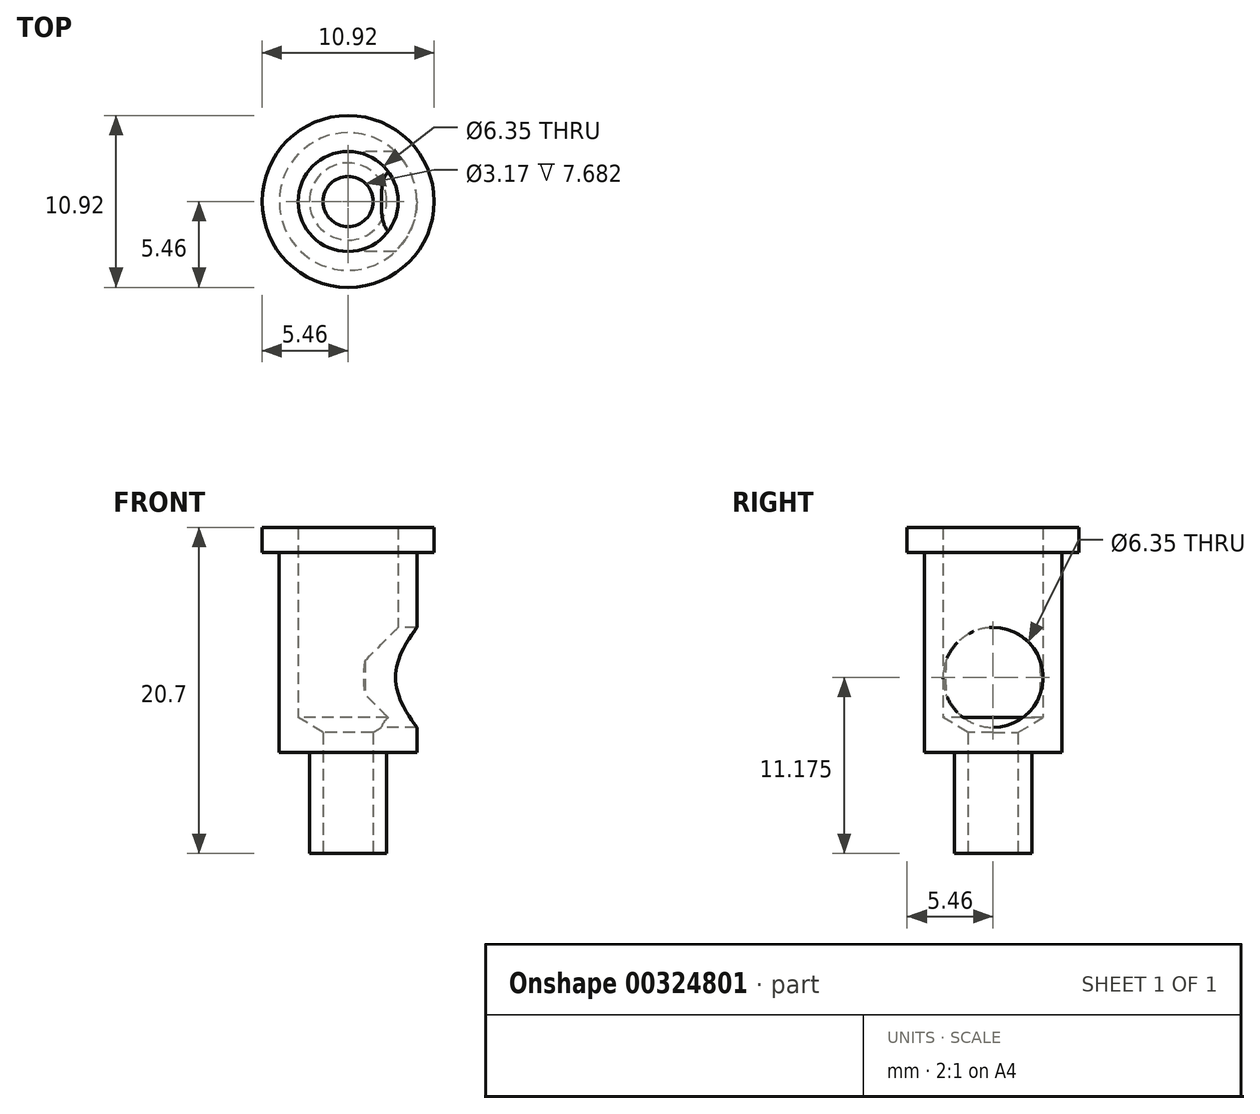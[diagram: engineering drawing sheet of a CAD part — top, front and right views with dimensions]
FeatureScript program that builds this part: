
annotation { "Feature Type Name" : "Feature", "Feature Type Description" : "" }
export const myFeature = defineFeature(function(context is Context, id is Id, definition is map)
    precondition{}
    {
        {
            var Q0;
            Q0=qCreatedBy(makeId("Top.planeOp"),FACE);
            var sketch = newSketch(context, id + "F0", { "sketchPlane" : qUnion([Q0])});
            skCircle(sketch, "E0", {"center": v(0, 0) * mm, "radius": 4.37 * mm});
            skSolve(sketch);
        }
        {
            var Q0;
            Q0=makeQuery(id+"F0.imprint","IMPRINT",FACE,{"disambiguationData":[TD([[makeQuery(id+"F0.imprint","IMPRINT",EDGE,{"derivedFrom":sQuery(id+"F0.wireOp",EDGE,"E0")}),1.0]])]});
            extrude(context, id + "F1", {"entities" : qUnion([Q0]), "depth" : 12.7 * mm, "offsetDistance" : 25.4 * mm});
        }
        {
            var Q0;
            Q0=makeQuery(id+"F1.opExtrude","CAP_FACE",FACE,{"disambiguationData":[OSD([sQuery(id+"F0.wireOp",EDGE,"E0")])],"isStart":false});
            var sketch = newSketch(context, id + "F2", { "sketchPlane" : qUnion([Q0])});
            skCircle(sketch, "E1", {"center": v(0, 0) * mm, "radius": 5.46 * mm});
            skSolve(sketch);
        }
        {
            var Q0;
            Q0=makeQuery(id+"F2.imprint","IMPRINT",FACE,{"disambiguationData":[TD([[makeQuery(id+"F2.imprint","IMPRINT",EDGE,{"derivedFrom":sQuery(id+"F2.wireOp",EDGE,"E1")}),1.0]])]});
            var Q1;
            Q1=makeQuery(id+"F2.imprint","IMPRINT",FACE,{"disambiguationData":[TD([[makeQuery(id+"F2.imprint","IMPRINT",EDGE,{"derivedFrom":makeQuery(id+"F1.opExtrude","CAP_EDGE",EDGE,{"disambiguationData":[OSD([sQuery(id+"F0.wireOp",EDGE,"E0")])],"isStart":false})}),1.0]])]});
            extrude(context, id + "F3", {"entities" : qUnion([Q0, Q1]), "operationType" : NewBodyOperationType.ADD, "depth" : 1.6 * mm, "offsetDistance" : 25.4 * mm});
        }
        {
            var Q0;
            Q0=makeQuery(id+"F3.opExtrude","CAP_FACE",FACE,{"disambiguationData":[OSD([sQuery(id+"F2.wireOp",EDGE,"E1")])],"isStart":false});
            var sketch = newSketch(context, id + "F4", { "sketchPlane" : qUnion([Q0])});
            skPoint(sketch, "E2", {"position": v(0, 0) * mm});
            skSolve(sketch);
        }
        {
            var Q0;
            Q0=sQuery(id+"F4.wireOp",VERTEX,"E2");
            var Q1;
            Q1=makeQuery(id+"F1.opExtrude","SWEPT_BODY",BODY,{"disambiguationData":[OSD([sQuery(id+"F0.wireOp",EDGE,"E0")])]});
            hole(context, id + "F5", {"style" : HoleStyle.SIMPLE, "endStyle" : HoleEndStyle.BLIND, "holeDiameter" : 6.35 * mm, "majorDiameter" : 6.35 * mm, "holeDepth" : 12.06 * mm, "tappedDepth" : 12.7 * mm, "tapClearance" : 3, "locations" : qUnion([Q0]), "scope" : qUnion([Q1])});
        }
        {
            var Q0;
            Q0=makeQuery(id+"F1.opExtrude","CAP_FACE",FACE,{"disambiguationData":[OSD([sQuery(id+"F0.wireOp",EDGE,"E0")])],"isStart":true});
            var sketch = newSketch(context, id + "F6", { "sketchPlane" : qUnion([Q0])});
            skCircle(sketch, "E3", {"center": v(0, 0) * mm, "radius": 2.45 * mm});
            skSolve(sketch);
        }
        {
            var Q0;
            Q0=makeQuery(id+"F6.imprint","IMPRINT",FACE,{"disambiguationData":[TD([[makeQuery(id+"F6.imprint","IMPRINT",EDGE,{"derivedFrom":sQuery(id+"F6.wireOp",EDGE,"E3")}),1.0]])]});
            extrude(context, id + "F7", {"entities" : qUnion([Q0]), "operationType" : NewBodyOperationType.ADD, "depth" : 6.4 * mm, "offsetDistance" : 25.4 * mm});
        }
        {
            var Q0;
            Q0=makeQuery(id+"F7.opExtrude","CAP_FACE",FACE,{"disambiguationData":[OSD([sQuery(id+"F6.wireOp",EDGE,"E3")])],"isStart":false});
            var sketch = newSketch(context, id + "F8", { "sketchPlane" : qUnion([Q0])});
            skCircle(sketch, "E4", {"center": v(0, 0) * mm, "radius": 1.59 * mm});
            skSolve(sketch);
        }
        {
            var Q0;
            Q0=makeQuery(id+"F8.imprint","IMPRINT",FACE,{"disambiguationData":[TD([[makeQuery(id+"F8.imprint","IMPRINT",EDGE,{"derivedFrom":sQuery(id+"F8.wireOp",EDGE,"E4")}),1.0]])]});
            extrude(context, id + "F9", {"entities" : qUnion([Q0]), "operationType" : NewBodyOperationType.REMOVE, "endBound" : BoundingType.THROUGH_ALL, "oppositeDirection" : true, "depth" : 25.4 * mm, "offsetDistance" : 25.4 * mm});
        }
        {
            var Q0;
            Q0=qCreatedBy(makeId("Right.planeOp"),FACE);
            cPlane(context, id + "F10", {"entities" : qUnion([Q0]), "cplaneType" : CPlaneType.OFFSET, "offset" : 4.37 * mm, "width" : 152.4 * mm, "height" : 152.4 * mm});
        }
        {
            var Q0;
            Q0=qCreatedBy(id+"F10.planeOp",FACE);
            var sketch = newSketch(context, id + "F11", { "sketchPlane" : qUnion([Q0])});
            skPoint(sketch, "E5", {"position": v(0, 4.78) * mm});
            skSolve(sketch);
        }
        {
            var Q0;
            Q0=sQuery(id+"F11.wireOp",VERTEX,"E5");
            var Q1;
            Q1=makeQuery(id+"F1.opExtrude","SWEPT_BODY",BODY,{"disambiguationData":[OSD([sQuery(id+"F0.wireOp",EDGE,"E0")])]});
            hole(context, id + "F12", {"style" : HoleStyle.SIMPLE, "endStyle" : HoleEndStyle.BLIND, "holeDiameter" : 6.35 * mm, "majorDiameter" : 6.35 * mm, "holeDepth" : 3.3 * mm, "tappedDepth" : 12.7 * mm, "tapClearance" : 3, "startFromSketch" : true, "locations" : qUnion([Q0]), "scope" : qUnion([Q1])});
        }
    });
